FCSTD DOCUMENT  (FreeCAD 0.18R4 (GitTag))
Label: second servo base
License: All rights reserved
LicenseURL: http://en.wikipedia.org/wiki/All_rights_reserved
objects: Sketcher::SketchObject×1
note: 1 computed .brp shape members not serialized (recipe doc carries the construction recipe); baked Part::Feature solids carry a one-line shape summary decoded from their .brp

FEATURE [Sketcher::SketchObject] Sketch002  label="Second servo base"
  sketch-geometry (5):
    g0: LineSegment StartX=-17 StartY=19 StartZ=0 EndX=17 EndY=19 EndZ=0
    g1: LineSegment StartX=17 StartY=19 StartZ=0 EndX=17 EndY=-19 EndZ=0
    g2: LineSegment StartX=17 StartY=-19 StartZ=0 EndX=-17 EndY=-19 EndZ=0
    g3: LineSegment StartX=-17 StartY=-19 StartZ=0 EndX=-17 EndY=19 EndZ=0
    g4: Circle CenterX=-0.0018 CenterY=-0.022057 CenterZ=0 NormalX=0 NormalY=0 NormalZ=1 AngleXU=0 Radius=0.98284
  constraints (10):
    c: Coincident(g0,g1)
    c: Coincident(g1,g2)
    c: Coincident(g2,g3)
    c: Coincident(g3,g0)
    c: Vertical(g3)
    c: DistanceX(g0,g0) = 34
    c: DistanceY(g1,g1) = 38
    c: Symmetric(g1,g0,g-1)
    c: Symmetric(g2,g1,g-2)
    c: Horizontal(g0)
